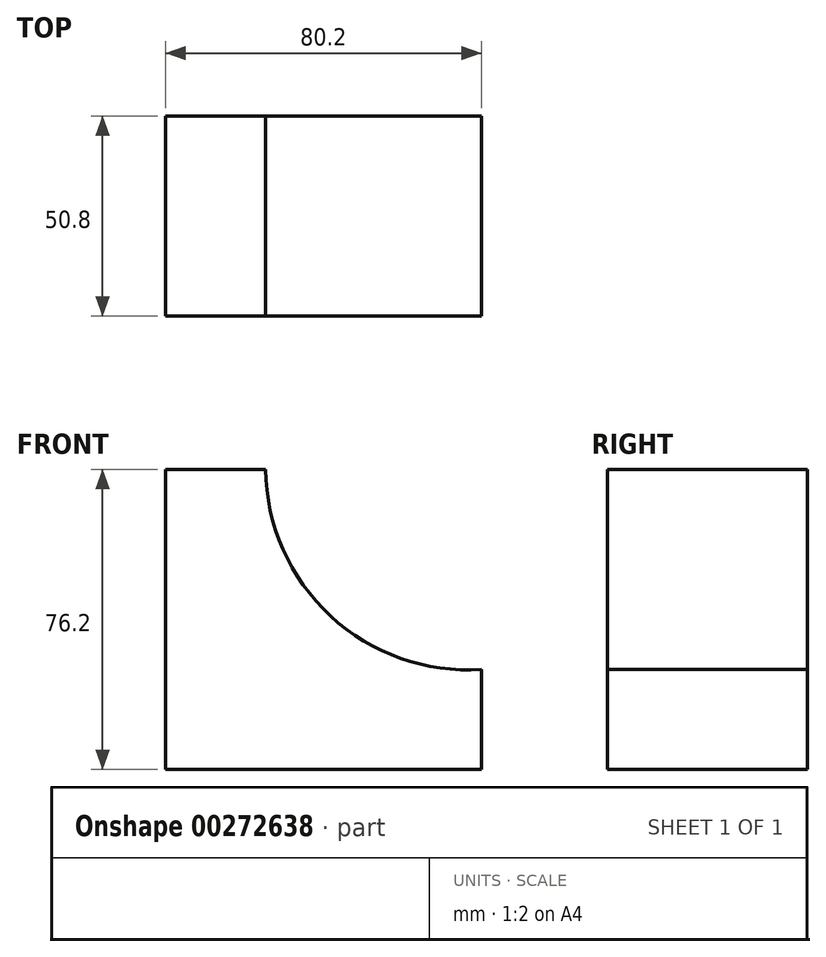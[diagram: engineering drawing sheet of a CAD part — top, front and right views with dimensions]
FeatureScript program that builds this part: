
annotation { "Feature Type Name" : "Feature", "Feature Type Description" : "" }
export const myFeature = defineFeature(function(context is Context, id is Id, definition is map)
    precondition{}
    {
        {
            var Q0;
            Q0=qCreatedBy(makeId("Front.planeOp"),FACE);
            var sketch = newSketch(context, id + "F0", { "sketchPlane" : qUnion([Q0])});
            skLineSegment(sketch, "E0", {"start": v(-46.97, 20.82) * mm, "end": v(-46.97, -55.38) * mm});
            skLineSegment(sketch, "E1", {"start": v(-46.97, -55.38) * mm, "end": v(33.23, -55.38) * mm});
            skLineSegment(sketch, "E2", {"start": v(33.23, -55.38) * mm, "end": v(33.23, -29.98) * mm});
            skLineSegment(sketch, "E3", {"start": v(-46.97, 20.82) * mm, "end": v(-21.57, 20.82) * mm});
            skArc(sketch, "E4", {"start": v(-21.57, 20.82) * mm, "mid": v(-5.11, -16.38) * mm, "end": v(33.23, -29.98) * mm});
            skSolve(sketch);
        }
        {
            var Q0;
            Q0=makeQuery(id+"F0.imprint","IMPRINT",FACE,{"disambiguationData":[TD([[makeQuery(id+"F0.imprint","IMPRINT",EDGE,{"derivedFrom":sQuery(id+"F0.wireOp",EDGE,"E0")}),1.0]])]});
            extrude(context, id + "F1", {"entities" : qUnion([Q0]), "depth" : 50.8 * mm});
        }
    });
